# Revit family: Lighting-Floodlights-GEWISS-STADIUMPRO3-LED-HIGH-POWER_3MODULE
name_source: partatom
category: Apparecchi per illuminazione
units: mm (PartAtom-declared; Revit-internal decimal feet)

## family parameters
Condiviso = No
Host = Superficie
Punto di calcolo locali = Sì
Quota connettore circolare = Usa diametro
Sorgente d'illuminazione = Sì
Taglio con vuoti quando caricato = No
Tipo di parte = Normale

## types (45) — shared parameters
Angolo inclinazione = 60.00°
Application = Indoor / Outdoor
Body = Die-cast aluminium -
Classification: = -
Colour = Graphite grey
Colour : = Polyester powder coated
Context = Professional sport lighting
Control System = See external supply unit
DIN 18032-3 certification = -
Device with reduced surface temperature = -
Driver = To be ordered separately
Driver Box = External
Driver failure rate = See external supply unit
Eletrical and lighting features = -
Emetti da lunghezza linea = 610 mm
External screw = Stainless steel
File diagramma fotometrico = generic
Filtro dei colori = 16777215
Fixing = Bracket
Gasket = Anti-aging silicone
General information = -
Glow Wire Test : = -
IDF = a6aa3e22-a2e7-464f-a96b-5eadfcc16f21
IDT = 0552d4b8-4f10-43b5-b8ac-94f59a03828d
IP degree = IP66
IPEA = -
Immagine tipo = StadiumPro3.jpg
Installationa and maintenance = -
Insulation class = I
LED Maintenance = Yes
Lifetime = L90B10(Tq25°C)=40.000h; L80B10(Tq25°C)=75.000h
Locking Hook = -
Lugnezza massima = 74 mm  [stored 0.242782 ft]
Luminaire = High power LED floodlight
Materials = -
Maximum surface exposed to the wind : = 0,36 m2
Mouting and installation = Lighting tower - Surface
Operating temperature : = -25 +50 °C
Optic : = T.I.R.Ex. Optical PMMA HT
Optic Maintenance = Not available
Optic and illuminating features = -
Overvoltage protection = See external supply unit
POSIZIONE = 80000
Photobiological Risk Class = -
Produttore = GEWISS S.p.A.
Prospetto di default = 1219 mm
Rated frequency (Hz) = See external supply unit
SEO = Floodlight
Shield type = Flat tempered glass 4mm
Shock resistance = IK08
Standard- = EN60598-1; EN60598-2-5; IEC 62471; IEC 62778
Standards and approvals = -
Stocking temperature = -
Supply voltage = See external supply unit
Technical sheet = https://www.gewiss.com
Tilt- = Rotation on bracket with integrated goniometer
Type of light source = LED - Not replaceable
URL = https://www.gewiss.com
Unified Glare Rating = ULOR = 0%
Unique digital code (Datamatrix) = Currently not present
Variazione temperatura colore lampada con luminosità attenuata = <Nessuno>
Version file RFA = 21.4
Warranty = 5 years
Wiring = Multipolar cable between floodlight and power supply
larghezza lampada = 50 mm  [stored 0.164042 ft]

## per-type parameters (varying)
| type | Catalogue | Color Rendering Index | Descrizione | Modello | Optic | Standard Deviation Colour Matching | Versions |
| GWP3331AB840 - STADIUM PRO 3M CL.I A1 CRI 80 4000K | LIGHTING | CRI 80 | STADIUM PRO 3M CL.I A1 CRI 80 4000K | GWP3331AB840 | Asymmetric 45° | SDCM = 3 | 4000K natural light |
| GWP3331AB857 - STADIUM PRO 3M CL.I A1 CRI 80 5700K | LIGHTING | CRI 80 | STADIUM PRO 3M CL.I A1 CRI 80 5700K | GWP3331AB857 | Asymmetric 45° | SDCM = 3 | 5700K cold light |
| GWP3331AM757 - STADIUM PRO 3M CL.I C5 CRI 70 5700K | LIGHTING | CRI70 | STADIUM PRO 3M CL.I C5 CRI 70 5700K | GWP3331AM757 | Circular 10° | SDCM = 5 | 5700K cold light |
| GWP3331AL957 - STADIUM PRO 3M CL.I C4 CRI 90 5700K | LIGHTING | CRI>90 TLCI>80 | STADIUM PRO 3M CL.I C4 CRI 90 5700K | GWP3331AL957 | Circular 15° | SDCM = 3 | 5700K cold light |
| GWP3331AG757 - STADIUM PRO 3M CL.I C2 CRI 70 5700K | E-MOBILITY | CRI70 | STADIUM PRO 3M CL.I C2 CRI 70 5700K | GWP3331AG757 | Circular 30° | SDCM = 5 | 5700K cold light |
| GWP3331AL840 - STADIUM PRO 3M CL.I C4 CRI 80 4000K | LIGHTING | CRI 80 | STADIUM PRO 3M CL.I C4 CRI 80 4000K | GWP3331AL840 | Circular 15° | SDCM = 3 | 4000K natural light |
| GWP3331AN957 - STADIUM PRO 3M CL.I C6 CRI 90 5700K | LIGHTING | CRI>90 TLCI>80 | STADIUM PRO 3M CL.I C6 CRI 90 5700K | GWP3331AN957 | Circular 8° | SDCM = 3 | 5700K cold light |
| GWP3331AA957 - STADIUM PRO 3M CL.I S1 CRI 90 5700K | LIGHTING | CRI>90 TLCI>80 | STADIUM PRO 3M CL.I S1 CRI 90 5700K | GWP3331AA957 | Elliptical 20°x80° | SDCM = 3 | 5700K cold light |
| GWP3331AF740 - STADIUM PRO 3M CL.I C1 CRI 70 4000K | LIGHTING | CRI70 | STADIUM PRO 3M CL.I C1 CRI 70 4000K | GWP3331AF740 | Circular 40° | SDCM = 5 | 4000K natural light |
| GWP3331AB957 - STADIUM PRO 3M CL.I A1 CRI 90 5700K | LIGHTING | CRI>90 TLCI>80 | STADIUM PRO 3M CL.I A1 CRI 90 5700K | GWP3331AB957 | Asymmetric 45° | SDCM = 3 | 5700K cold light |
| GWP3331AL757 - STADIUM PRO 3M CL.I C4 CRI 70 5700K | LIGHTING | CRI70 | STADIUM PRO 3M CL.I C4 CRI 70 5700K | GWP3331AL757 | Circular 15° | SDCM = 5 | 5700K cold light |
| GWP3331AA857 - STADIUM PRO 3M CL.I S1 CRI 80 5700K | LIGHTING | CRI 80 | STADIUM PRO 3M CL.I S1 CRI 80 5700K | GWP3331AA857 | Elliptical 20°x80° | SDCM = 3 | 5700K cold light |
| GWP3331AH740 - STADIUM PRO 3M CL.I C3 CRI 70 4000K | LIGHTING | CRI70 | STADIUM PRO 3M CL.I C3 CRI 70 4000K | GWP3331AH740 | Circular 20° | SDCM = 5 | 4000K natural light |
| GWP3331AG857 - STADIUM PRO 3M CL.I C2 CRI 80 5700K | E-MOBILITY | CRI 80 | STADIUM PRO 3M CL.I C2 CRI 80 5700K | GWP3331AG857 | Circular 30° | SDCM = 3 | 5700K cold light |
| GWP3331AM957 - STADIUM PRO 3M CL.I C5 CRI 90 5700K | LIGHTING | CRI>90 TLCI>80 | STADIUM PRO 3M CL.I C5 CRI 90 5700K | GWP3331AM957 | Circular 10° | SDCM = 3 | 5700K cold light |
| GWP3331AH840 - STADIUM PRO 3M CL.I C3 CRI 80 4000K | LIGHTING | CRI 80 | STADIUM PRO 3M CL.I C3 CRI 80 4000K | GWP3331AH840 | Circular 20° | SDCM = 3 | 4000K natural light |
| GWP3331AM840 - STADIUM PRO 3M CL.I C5 CRI 80 4000K | LIGHTING | CRI 80 | STADIUM PRO 3M CL.I C5 CRI 80 4000K | GWP3331AM840 | Circular 10° | SDCM = 3 | 4000K natural light |
| GWP3331AH757 - STADIUM PRO 3M CL.I C3 CRI 70 5700K | LIGHTING | CRI70 | STADIUM PRO 3M CL.I C3 CRI 70 5700K | GWP3331AH757 | Circular 20° | SDCM = 5 | 5700K cold light |
| GWP3331AB740 - STADIUM PRO 3M CL.I A1 CRI 70 4000K | LIGHTING | CRI70 | STADIUM PRO 3M CL.I A1 CRI 70 4000K | GWP3331AB740 | Asymmetric 45° | SDCM = 5 | 4000K natural light |
| GWP3331AN757 - STADIUM PRO 3M CL.I C6 CRI 70 5700K | LIGHTING | CRI70 | STADIUM PRO 3M CL.I C6 CRI 70 5700K | GWP3331AN757 | Circular 8° | SDCM = 5 | 5700K cold light |
| GWP3331AA757 - STADIUM PRO 3M CL.I S1 CRI 70 5700K | LIGHTING | CRI70 | STADIUM PRO 3M CL.I S1 CRI 70 5700K | GWP3331AA757 | Elliptical 20°x80° | SDCM = 5 | 5700K cold light |
| GWP3331AC840 - STADIUM PRO 3M CL.I A2 CRI 80 4000K | LIGHTING | CRI 80 | STADIUM PRO 3M CL.I A2 CRI 80 4000K | GWP3331AC840 | Asymmetric 60° | SDCM = 3 | 4000K natural light |
| GWP3331AB757 - STADIUM PRO 3M CL.I A1 CRI 70 5700K | LIGHTING | CRI70 | STADIUM PRO 3M CL.I A1 CRI 70 5700K | GWP3331AB757 | Asymmetric 45° | SDCM = 5 | 5700K cold light |
| GWP3331AA840 - STADIUM PRO 3M CL.I S1 CRI 80 4000K | LIGHTING | CRI 80 | STADIUM PRO 3M CL.I S1 CRI 80 4000K | GWP3331AA840 | Elliptical 20°x80° | SDCM = 3 | 4000K natural light |
| GWP3331AN840 - STADIUM PRO 3M CL.I C6 CRI 80 4000K | LIGHTING | CRI 80 | STADIUM PRO 3M CL.I C6 CRI 80 4000K | GWP3331AN840 | Circular 8° | SDCM = 3 | 4000K natural light |
| GWP3331AF757 - STADIUM PRO 3M CL.I C1 CRI 70 5700K | LIGHTING | CRI70 | STADIUM PRO 3M CL.I C1 CRI 70 5700K | GWP3331AF757 | Circular 40° | SDCM = 5 | 5700K cold light |
| GWP3331AM740 - STADIUM PRO 3M CL.I C5 CRI 70 4000K | LIGHTING | CRI70 | STADIUM PRO 3M CL.I C5 CRI 70 4000K | GWP3331AM740 | Circular 10° | SDCM = 5 | 4000K natural light |
| GWP3331AG740 - STADIUM PRO 3M CL.I C2 CRI 70 4000K | E-MOBILITY | CRI70 | STADIUM PRO 3M CL.I C2 CRI 70 4000K | GWP3331AG740 | Circular 30° | SDCM = 5 | 4000K natural light |
| GWP3331AN857 - STADIUM PRO 3M CL.I C6 CRI 80 5700K | LIGHTING | CRI 80 | STADIUM PRO 3M CL.I C6 CRI 80 5700K | GWP3331AN857 | Circular 8° | SDCM = 3 | 5700K cold light |
| GWP3331AG840 - STADIUM PRO 3M CL.I C2 CRI 80 4000K | E-MOBILITY | CRI 80 | STADIUM PRO 3M CL.I C2 CRI 80 4000K | GWP3331AG840 | Circular 30° | SDCM = 3 | 4000K natural light |
| GWP3331AA740 - STADIUM PRO 3M CL.I S1 CRI 70 4000K | LIGHTING | CRI70 | STADIUM PRO 3M CL.I S1 CRI 70 4000K | GWP3331AA740 | Elliptical 20°x80° | SDCM = 5 | 4000K natural light |
| GWP3331AF957 - STADIUM PRO 3M CL.I C1 CRI 90 5700K | LIGHTING | CRI>90 TLCI>80 | STADIUM PRO 3M CL.I C1 CRI 90 5700K | GWP3331AF957 | Circular 40° | SDCM = 3 | 5700K cold light |
| GWP3331AF840 - STADIUM PRO 3M CL.I C1 CRI 80 4000K | LIGHTING | CRI 80 | STADIUM PRO 3M CL.I C1 CRI 80 4000K | GWP3331AF840 | Circular 40° | SDCM = 3 | 4000K natural light |
| GWP3331AL740 - STADIUM PRO 3M CL.I C4 CRI 70 4000K | LIGHTING | CRI70 | STADIUM PRO 3M CL.I C4 CRI 70 4000K | GWP3331AL740 | Circular 15° | SDCM = 5 | 4000K natural light |
| GWP3331AG957 - STADIUM PRO 3M CL.I C2 CRI 90 5700K | E-MOBILITY | CRI>90 TLCI>80 | STADIUM PRO 3M CL.I C2 CRI 90 5700K | GWP3331AG957 | Circular 30° | SDCM = 3 | 5700K cold light |
| GWP3331AF857 - STADIUM PRO 3M CL.I C1 CRI 80 5700K | LIGHTING | CRI 80 | STADIUM PRO 3M CL.I C1 CRI 80 5700K | GWP3331AF857 | Circular 40° | SDCM = 3 | 5700K cold light |
| GWP3331AH957 - STADIUM PRO 3M CL.I C3 CRI 90 5700K | LIGHTING | CRI>90 TLCI>80 | STADIUM PRO 3M CL.I C3 CRI 90 5700K | GWP3331AH957 | Circular 20° | SDCM = 3 | 5700K cold light |
| GWP3331AL857 - STADIUM PRO 3M CL.I C4 CRI 80 5700K | LIGHTING | CRI 80 | STADIUM PRO 3M CL.I C4 CRI 80 5700K | GWP3331AL857 | Circular 15° | SDCM = 3 | 5700K cold light |
| GWP3331AC957 - STADIUM PRO 3M CL.I A2 CRI 90 5700K | LIGHTING | CRI>90 TLCI>80 | STADIUM PRO 3M CL.I A2 CRI 90 5700K | GWP3331AC957 | Asymmetric 60° | SDCM = 3 | 5700K cold light |
| GWP3331AN740 - STADIUM PRO 3M CL.I C6 CRI 70 4000K | LIGHTING | CRI70 | STADIUM PRO 3M CL.I C6 CRI 70 4000K | GWP3331AN740 | Circular 8° | SDCM = 5 | 4000K natural light |
| GWP3331AC757 - STADIUM PRO 3M CL.I A2 CRI 70 5700K | LIGHTING | CRI70 | STADIUM PRO 3M CL.I A2 CRI 70 5700K | GWP3331AC757 | Asymmetric 60° | SDCM = 5 | 5700K cold light |
| GWP3331AH857 - STADIUM PRO 3M CL.I C3 CRI 80 5700K | LIGHTING | CRI 80 | STADIUM PRO 3M CL.I C3 CRI 80 5700K | GWP3331AH857 | Circular 20° | SDCM = 3 | 5700K cold light |
| GWP3331AC857 - STADIUM PRO 3M CL.I A2 CRI 80 5700K | LIGHTING | CRI 80 | STADIUM PRO 3M CL.I A2 CRI 80 5700K | GWP3331AC857 | Asymmetric 60° | SDCM = 3 | 5700K cold light |
| GWP3331AC740 - STADIUM PRO 3M CL.I A2 CRI 70 4000K | LIGHTING | CRI70 | STADIUM PRO 3M CL.I A2 CRI 70 4000K | GWP3331AC740 | Asymmetric 60° | SDCM = 5 | 4000K natural light |
| GWP3331AM857 - STADIUM PRO 3M CL.I C5 CRI 80 5700K | LIGHTING | CRI 80 | STADIUM PRO 3M CL.I C5 CRI 80 5700K | GWP3331AM857 | Circular 10° | SDCM = 3 | 5700K cold light |

note: [stored X ft] marks values corroborated as IEEE doubles in the binary element streams (Revit-internal decimal feet)
